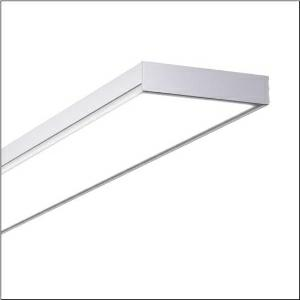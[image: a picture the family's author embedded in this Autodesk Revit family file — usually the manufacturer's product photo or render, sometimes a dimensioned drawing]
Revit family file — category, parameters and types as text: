
# Revit family: apollon_r__31_51mp26wm2341e_4571
name_source: partatom
category: Lighting Fixtures
units: mm (PartAtom-declared; Revit-internal decimal feet)

## family parameters
Cut with Voids When Loaded = No
Host = Face
Light Source = No
Part Type = Normal
Room Calculation Point = No
Round Connector Dimension = Use Diameter
Shared = No

## types (1)
- Apollon® 31 (1 x LED, 4400 lm, 33 W, 3000K)
    Apparent Load = 33 VA
    CIE Flux Codes = 61 87 97 97 100
    Color Rendering = 80
    Color Temperature = 3000K
    Default Elevation = 1800 mm
    Description = Apollon® 31, office luminaire, primary optical cover: micro prismatic cover, of PMMA, light emission: direct distribution, primary light characteristic: symmetric, installation type: surface-mounted, LED, rated luminous flux: 4.400lm, luminous efficacy: 133lm/W, light colour: 830, colour temperature: 3000K, control gear: ECG Multilumen, with terminal, 3-pole, mains connection: 220..240V, AC, 50/60Hz, rated input power: 33W, housing, of sheet steel, coil coated, metallic grey (RAL 9006), length: 1.545mm, width: 200mm, height: 44mm, protection rating (complete): IP20, insulation class (complete): insulation class II (safety insulation), certification: CE, impact resistance: IK02, permissible operating ambient temperature: -20..+40°C, packaging unit: 1 piece
    Height = 44 mm
    Lamp = 1 x LED
    Lamp Light Flux = 4400 lm
    Lamp Power = 33 W
    Lamp count = 1
    Length = 1545 mm
    Luminous efficacy = 133 lm/W
    Manufacturer = Siteco
    ModVariant = No
    Model = 51MP26WM2341E
    Mounting Place = Ceiling
    Mounting Type = Surface mounted
    Number of Poles = 1
    OnlyDefault = Yes
    Power Factor = 1
    Product Name = Apollon® 31
    Product group = office luminaire | ceiling mounted
    ProductGroupID = 302
    Protection Class = Protection class II
    Protection Degree = IP 20
    RLX_Detail_Level = 1
    RlxData = <blob elided: 24077 chars, md5=6ead9ddd>
    Socket = socket
    Standby Power = 0 W
    System Light Flux = 4400 lm
    System Power = 33 W
    Type Comments = Product without accessories
    Type Image = l_1007091.jpg
    URL = http://relux.com
    VarID = ---
    Voltage = 0 V
    Weight = 0.00 kg
    Width = 200 mm  [stored 0.656168 ft]

note: [stored X ft] marks values corroborated as IEEE doubles in the binary element streams (Revit-internal decimal feet)

## geometry (parser evidence)
native form markers: Blend x4, Sweep x14
no freeform markers — native parametric forms only
